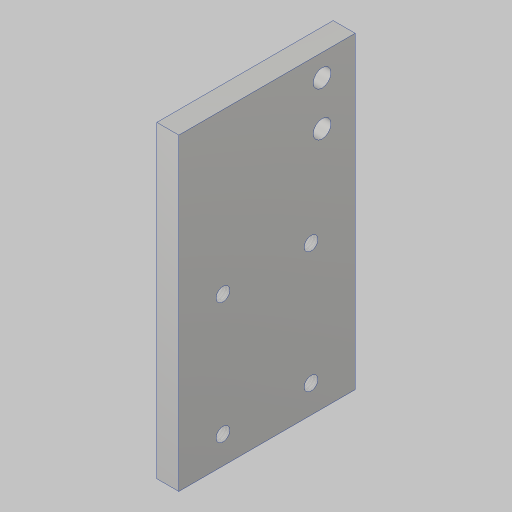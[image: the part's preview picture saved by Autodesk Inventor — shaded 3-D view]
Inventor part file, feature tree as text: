
AUTODESK INVENTOR PART (.ipt)
format: ipt  version: 2023.5 (Build 275446000, 446)  size: 114,688 bytes
history: native  units: in
note: dims shown in document units (in); Inventor stores cm internally (conversion verified against a paired STEP export)
features: sketch x2, hole x2, extrude x1
ambient origin geometry x8: Origin, YZ Plane, XZ Plane, XY Plane, X Axis, Y Axis, Z Axis, Center Point
bodies: Solid1 (feature_tree)
feature tree (5):
  extrude  "Extrusion1"  Depth=2.0in
  sketch  "Sketch2"  dims[d2=0.25in d3=0.0in d4=1.0in d5=1.375in d6=0.313in d7=0.5in d9=0.156in d10=0.38in d11=0.507in d12=0.25in d13=0.5635in d14=1.0in d15=0.8108in d16=0.201in d17=0.38in d18=0.385in d19=0.25in d20=0.5635in d21=1.0in d22=0.8108in d23=0.25in d24=0.375in]
  hole  "Hole1"  [1 undecoded]
  hole  "Hole2"  [1 undecoded]
  sketch  "Sketch1"  dims[d0=3.5in d1=2.0in]
note: 2 required parameter values undecoded (feature->parameter linkage not recoverable at this tier; creation-order binding heuristic only, values carry confidence <= 0.55)
